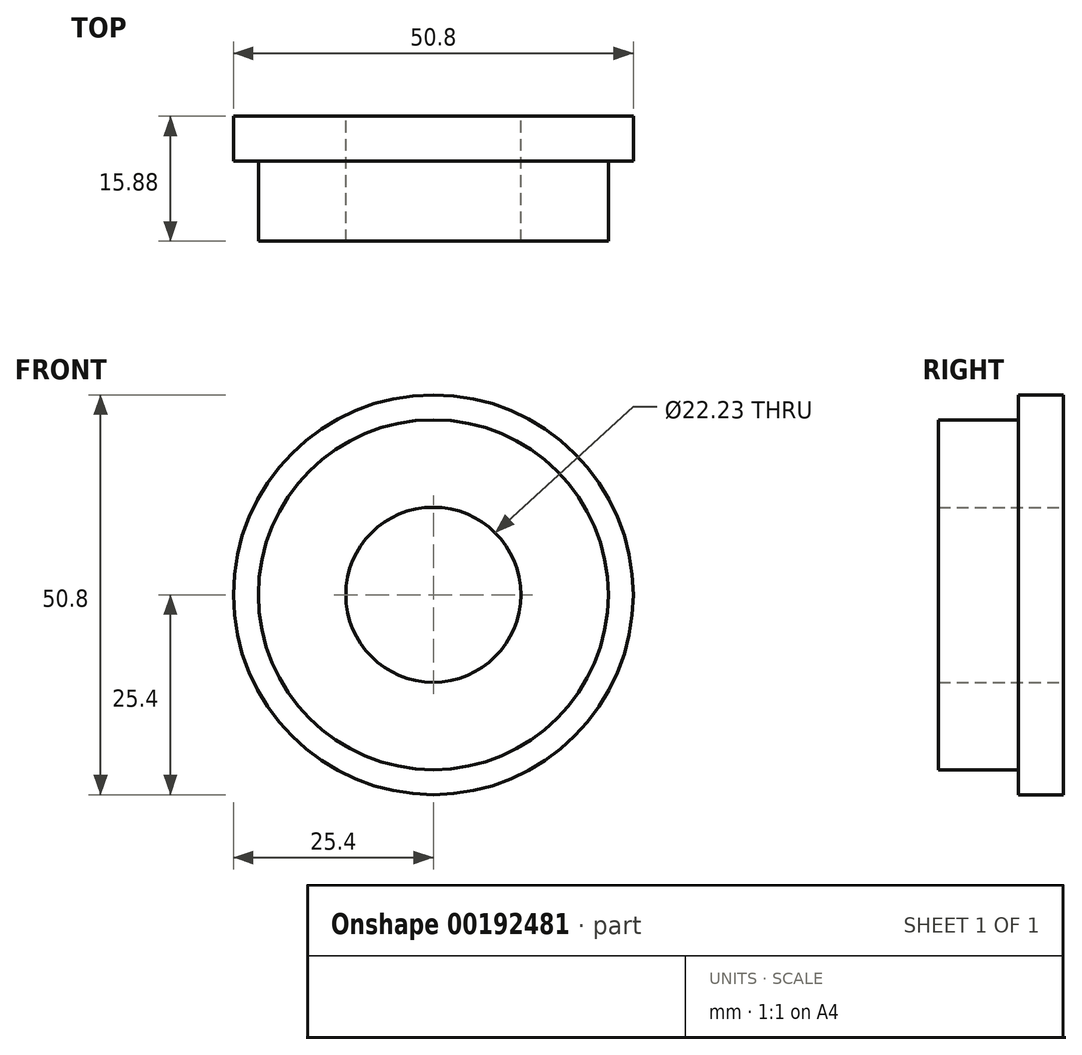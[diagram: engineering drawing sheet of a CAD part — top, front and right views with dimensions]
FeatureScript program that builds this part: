
annotation { "Feature Type Name" : "Feature", "Feature Type Description" : "" }
export const myFeature = defineFeature(function(context is Context, id is Id, definition is map)
    precondition{}
    {
        {
            var Q0;
            Q0=qCreatedBy(makeId("Front.planeOp"),FACE);
            var sketch = newSketch(context, id + "F0", { "sketchPlane" : qUnion([Q0])});
            skCircle(sketch, "E0", {"center": v(0, 0) * mm, "radius": 25.4 * mm});
            skCircle(sketch, "E1", {"center": v(0, 0) * mm, "radius": 11.11 * mm});
            skSolve(sketch);
        }
        {
            var Q0;
            Q0 = qSketchRegion(id + "F0", true);
            extrude(context, id + "F1", {"entities" : qUnion([Q0]), "depth" : 15.88 * mm});
        }
        {
            var Q0;
            Q0=makeQuery(id+"F1.opExtrude","CAP_FACE",FACE,{"disambiguationData":[OSD([sQuery(id+"F0.wireOp",EDGE,"E0"),sQuery(id+"F0.wireOp",EDGE,"E1")])],"isStart":false});
            var sketch = newSketch(context, id + "F2", { "sketchPlane" : qUnion([Q0])});
            skCircle(sketch, "E2", {"center": v(0, 0) * mm, "radius": 22.23 * mm});
            skCircle(sketch, "E3", {"center": v(0, 0) * mm, "radius": 25.4 * mm});
            skSolve(sketch);
        }
        {
            var Q0;
            Q0=makeQuery(id+"F2.imprint","IMPRINT",FACE,{"disambiguationData":[TD([[makeQuery(id+"F2.imprint","IMPRINT",EDGE,{"derivedFrom":sQuery(id+"F2.wireOp",EDGE,"E2")}),-1.0]])]});
            extrude(context, id + "F3", {"entities" : qUnion([Q0]), "operationType" : NewBodyOperationType.REMOVE, "oppositeDirection" : true, "depth" : 10.16 * mm});
        }
    });
